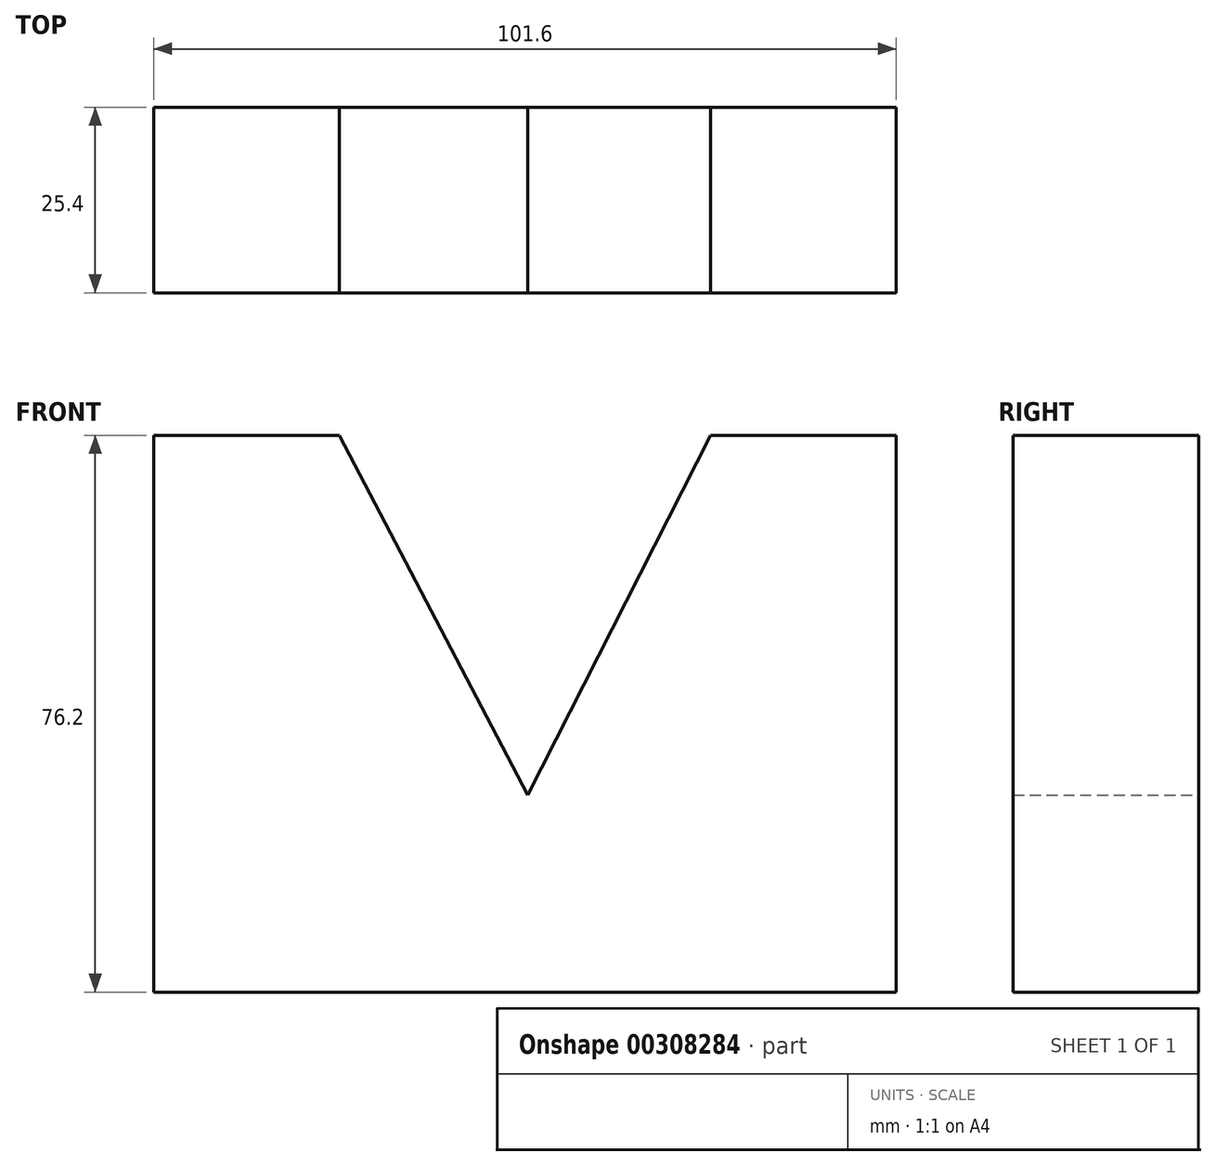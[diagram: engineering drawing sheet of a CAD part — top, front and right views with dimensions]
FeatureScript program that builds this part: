
annotation { "Feature Type Name" : "Feature", "Feature Type Description" : "" }
export const myFeature = defineFeature(function(context is Context, id is Id, definition is map)
    precondition{}
    {
        {
            var Q0;
            Q0=qCreatedBy(makeId("Front.planeOp"),FACE);
            var sketch = newSketch(context, id + "F0", { "sketchPlane" : qUnion([Q0])});
            skLineSegment(sketch, "E0", {"start": v(-51.18, -43.3) * mm, "end": v(-51.18, 32.9) * mm});
            skLineSegment(sketch, "E1", {"start": v(-51.18, 32.9) * mm, "end": v(-25.78, 32.9) * mm});
            skLineSegment(sketch, "E2", {"start": v(-51.18, -43.3) * mm, "end": v(50.42, -43.3) * mm});
            skLineSegment(sketch, "E3", {"start": v(50.42, -43.3) * mm, "end": v(50.42, 32.9) * mm});
            skLineSegment(sketch, "E4", {"start": v(50.42, 32.9) * mm, "end": v(25.02, 32.9) * mm});
            skLineSegment(sketch, "E5", {"start": v(25.02, 32.9) * mm, "end": v(0, -16.36) * mm});
            skLineSegment(sketch, "E6", {"start": v(0, -16.36) * mm, "end": v(-25.78, 32.9) * mm});
            skSolve(sketch);
        }
        {
            var Q0;
            Q0 = qSketchRegion(id + "F0", true);
            var Q1;
            Q1=makeQuery(id+"F0.imprint","IMPRINT",FACE,{"disambiguationData":[TD([[makeQuery(id+"F0.imprint","IMPRINT",EDGE,{"derivedFrom":sQuery(id+"F0.wireOp",EDGE,"E0")}),-1.0]])]});
            extrude(context, id + "F1", {"entities" : qUnion([Q0, Q1]), "depth" : 25.4 * mm});
        }
    });
